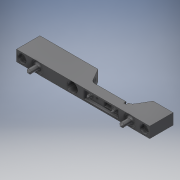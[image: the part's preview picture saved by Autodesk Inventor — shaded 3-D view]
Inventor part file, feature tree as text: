
AUTODESK INVENTOR PART (.ipt)
format: ipt  version: 2018 (Build 220112000, 112)  size: 411,136 bytes
history: native  units: mm
features: sketch x19, extrude x14, projected_geometry x14, hole x5, chamfer x3, fillet x3, draft x2, plane x1
ambient origin geometry x8: Origin, YZ Plane, XZ Plane, XY Plane, X Axis, Y Axis, Z Axis, Center Point
bodies: Solid1 (feature_tree)
feature tree (61):
  extrude  "Extrusion1"  Depth=7.0mm
  extrude  "Extrusion2"  Depth=4.2mm
  extrude  "Extrusion3"  Depth=6.4mm
  extrude  "Extrusion4"  TaperAngle=0.0deg  [1 undecoded]
  extrude  "Extrusion5"  Depth=5.2mm
  hole  "Hole1"  [1 undecoded]
  hole  "Hole2"  [1 undecoded]
  extrude  "Extrusion8"  Depth=2.4mm
  chamfer  "Chamfer1"  Distance=2.4mm
  plane  "Work Plane2"
  fillet  "Fillet1"  Radius=3.5mm
  extrude  "Extrusion10"  Depth=3.5mm
  sketch  "Sketch14"  dims[d42=15.4mm]
  hole  "Hole3"  [1 undecoded]
  extrude  "Extrusion11"  Depth=1.0mm TaperAngle=0.0deg
  chamfer  "Chamfer3"  Distance=1.0mm Angle=45.0deg
  chamfer  "Chamfer4"  Distance=0.8mm
  extrude  "Extrusion12"  Depth=71.4mm
  extrude  "Extrusion14"  Depth=6.0mm
  hole  "Hole4"  [1 undecoded]
  extrude  "Extrusion15"  Depth=1.4mm TaperAngle=45.0deg
  hole  "Hole5"  [1 undecoded]
  extrude  "Extrusion17"  Depth=7.0mm TaperAngle=0.0deg
  extrude  "Extrusion18"  TaperAngle=45.0deg  [1 undecoded]
  draft  "FaceDraft2"
  draft  "FaceDraft3"
  fillet  "Fillet3"  Radius=7.0mm
  extrude  "Extrusion19"  TaperAngle=45.0deg  [1 undecoded]
  fillet  "Fillet4"  Radius=1.5mm
  sketch  "Sketch1"  dims[d0=22.8mm d1=7.0mm]
  sketch  "Sketch2"  dims[d2=6.0mm d3=0.0mm d4=4.2mm]
  sketch  "Sketch3"  dims[d5=4.5mm d6=6.4mm]
  projected_geometry  "Projected Loop1"
  sketch  "Sketch4"  dims[d7=6.0mm d8=0.0mm d11=0.0mm]
  projected_geometry  "Projected Loop2"
  sketch  "Sketch5"  dims[d12=0.9mm d13=5.2mm]
  sketch  "Sketch6"  dims[d14=22.0mm d15=2.0mm d16=0.0mm]
  projected_geometry  "Projected Loop3"
  sketch  "Sketch8"  dims[d17=14.0mm d18=2.9mm d19=0.0mm]
  sketch  "Sketch9"  dims[d20=12.9mm d21=5.0mm d22=2.4mm d23=0.0mm]
  sketch  "Sketch13"  dims[d24=0.5mm d25=6.0mm d26=3.023mm d27=2.0mm d28=14.3117mm d29=2.4mm d30=0.0mm d41=3.5mm]
  projected_geometry  "Projected Loop11"
  sketch  "Sketch15"  dims[d43=1.181mm d44=3.048mm d45=3.023mm d46=2.0mm d47=14.3117mm d48=4.636mm d49=0.0mm d50=3.5mm]
  projected_geometry  "Projected Loop12"
  sketch  "Sketch16"  dims[d51=16.1mm d52=3.3mm]
  projected_geometry  "Projected Loop13"
  sketch  "Sketch18"  dims[d53=2.0mm d54=2.8mm d55=0.0mm d56=1.0mm d57=2.0mm d58=45.0deg d67=-3.5mm d74=0.8mm]
  projected_geometry  "Projected Loop15"
  sketch  "Sketch19"  dims[d75=38.8mm d76=71.4mm]
  projected_geometry  "Projected Loop16"
  sketch  "Sketch20"  dims[d77=15.0mm d78=0.0mm]
  projected_geometry  "Projected Loop17"
  sketch  "Sketch21"  dims[d80=6.5mm d81=6.0mm d82=3.023mm d83=2.0mm d84=14.3117mm d85=12.0mm d86=0.0mm d87=6.0mm]
  projected_geometry  "Projected Loop18"
  sketch  "Sketch23"  dims[d88=65.4mm d89=2.8mm]
  projected_geometry  "Projected Loop20"
  sketch  "Sketch24"  dims[d90=6.188mm d91=0.0mm d92=1.4mm d93=2.0mm d94=45.0deg]
  projected_geometry  "Projected Loop21"
  sketch  "Sketch25"  dims[d95=0.25mm d96=2.0mm d97=45.0deg d98=6.0mm d99=0.0mm d106=7.0mm d107=0.0mm d108=45.0deg d109=2.9mm d110=6.0mm d111=5.5mm d112=2.5mm d113=14.3117mm d114=12.0mm d115=0.0mm d116=7.0mm d117=0.0mm d118=45.0deg d119=2.9mm d120=6.0mm d121=5.5mm d122=2.5mm d123=14.3117mm d124=12.0mm d125=0.0mm d129=1.5mm d130=1.5mm d131=0.0mm d132=18.0mm d133=1.5mm d134=0.0mm d135=30.0deg d136=30.0deg d137=3.0mm d138=6.0mm d139=6.0mm d140=1.0mm d141=0.0mm d142=1.0mm d143=7.5mm]
  projected_geometry  "Projected Loop22"
  projected_geometry  "Projected Loop23"
note: 8 required parameter values undecoded (feature->parameter linkage not recoverable at this tier; creation-order binding heuristic only, values carry confidence <= 0.55)
